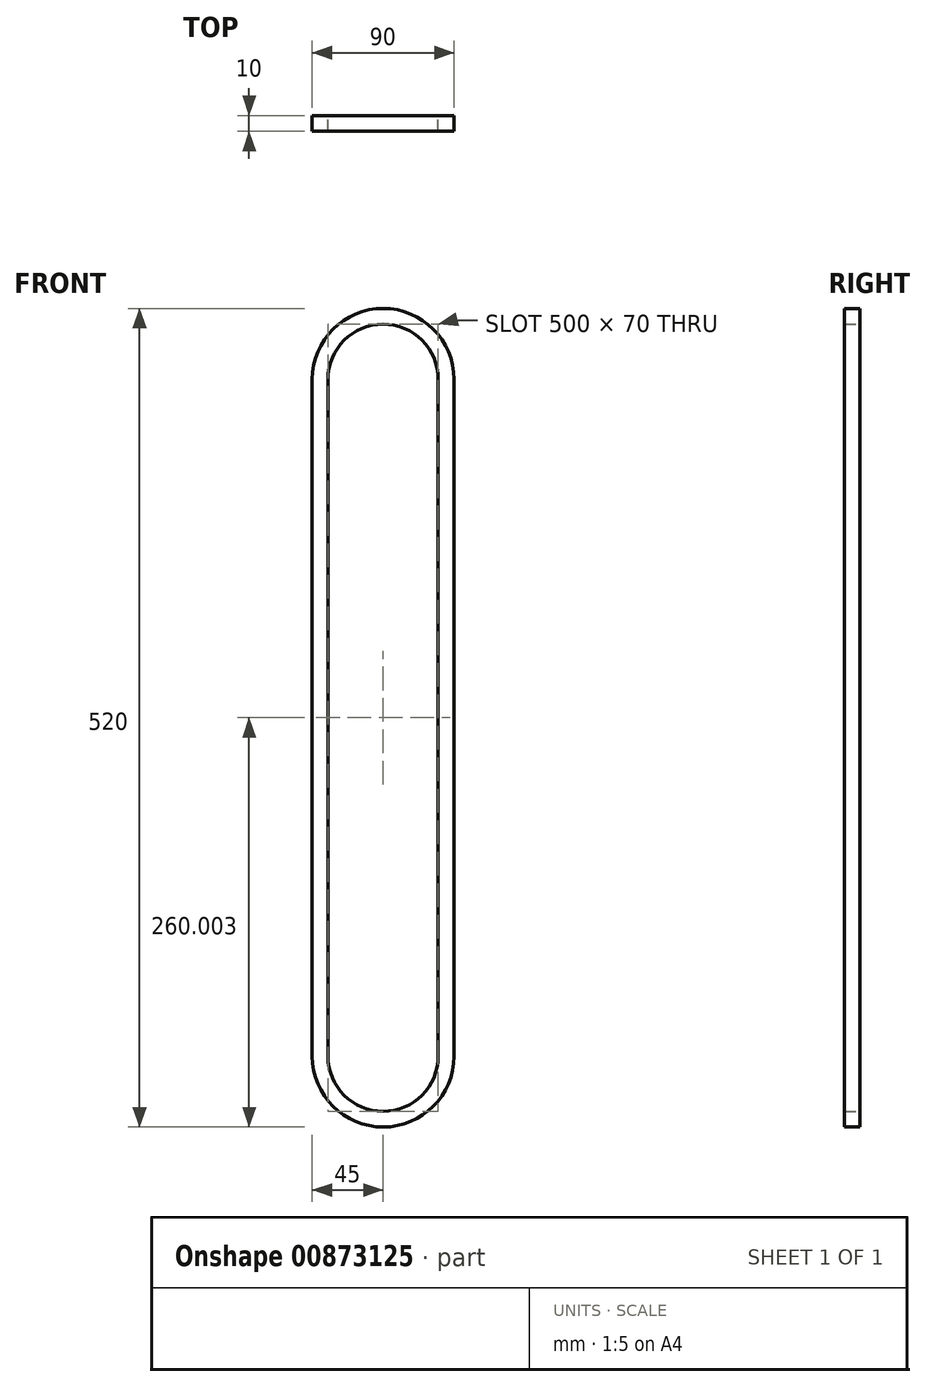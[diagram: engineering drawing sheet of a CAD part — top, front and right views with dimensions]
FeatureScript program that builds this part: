
annotation { "Feature Type Name" : "Feature", "Feature Type Description" : "" }
export const myFeature = defineFeature(function(context is Context, id is Id, definition is map)
    precondition{}
    {
        {
            var Q0;
            Q0=qCreatedBy(makeId("Front.planeOp"),FACE);
            var sketch = newSketch(context, id + "F0", { "sketchPlane" : qUnion([Q0])});
            skArc(sketch, "E0", {"start": v(35, 363.08) * mm, "mid": v(0, 398.08) * mm, "end": v(-35, 363.08) * mm});
            skLineSegment(sketch, "E1", {"start": v(-35, 363.08) * mm, "end": v(-35, -66.92) * mm});
            skLineSegment(sketch, "E2", {"start": v(35, 363.08) * mm, "end": v(35, -66.92) * mm});
            skPoint(sketch, "E3.center.orphan", {"position": v(0, -66.92) * mm});
            skArc(sketch, "E4", {"start": v(-35, -66.92) * mm, "mid": v(0, -101.92) * mm, "end": v(35, -66.92) * mm});
            skArc(sketch, "E5", {"start": v(45, 363.08) * mm, "mid": v(0, 408.08) * mm, "end": v(-45, 363.08) * mm});
            skLineSegment(sketch, "E6", {"start": v(45, 363.08) * mm, "end": v(45, -66.92) * mm});
            skLineSegment(sketch, "E7", {"start": v(-45, 363.08) * mm, "end": v(-45, -66.92) * mm});
            skArc(sketch, "E8", {"start": v(-45, -66.92) * mm, "mid": v(0, -111.92) * mm, "end": v(45, -66.92) * mm});
            skSolve(sketch);
        }
        {
            var Q0;
            Q0 = qSketchRegion(id + "F0", true);
            extrude(context, id + "F1", {"entities" : qUnion([Q0]), "depth" : 10 * mm, "offsetDistance" : 25 * mm});
        }
    });
